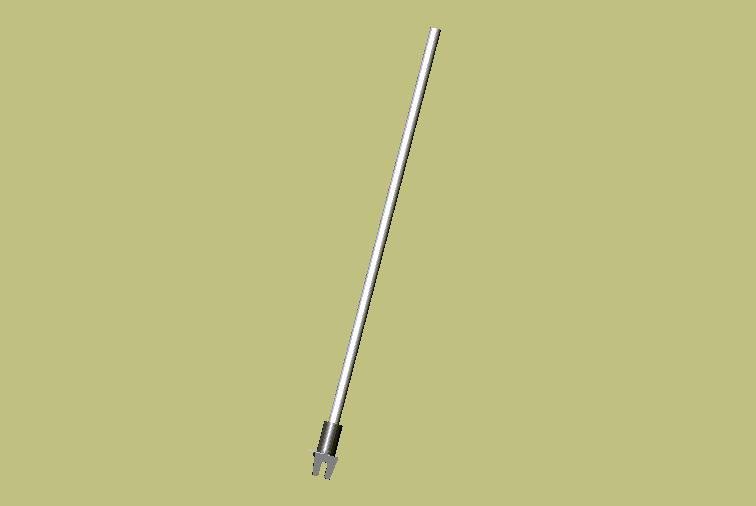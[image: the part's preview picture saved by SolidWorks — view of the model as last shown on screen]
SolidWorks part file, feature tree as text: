
SOLIDWORKS PART (.sldprt)
format: sldprt  version: not decoded by parser v0  size: 140,800 bytes
history: native  units: mm
features: sketch x5, plane x3, extrude x3, cut_extrude x2, material x1, fillet x1 (+8 scaffold rows collapsed)
feature tree (23):
  scaffold x8  (default folders/planes/origin — collapsed)
  material  "Matériau <non spécifié>"
  plane  "Plane1"
  plane  "Plane2"
  plane  "Plane3"
  sketch  "Esquisse1"  dims[D1=7.0mm D2=2.0mm]
  extrude  "Base-Extrusion"  Depth=12mm
  sketch  "Esquisse2"  dims[D1=4.0mm D2=3.0mm]
  extrude  "Boss.-Extru.1"  Depth=150mm
  sketch  "Esquisse3"  dims[D1=4.0mm D2=10.0mm D3=1.5mm D4=1.5mm]
  extrude  "Boss.-Extru.2"  Depth=9mm
  fillet  "Congé1"  Radius=4mm
  sketch  "Esquisse4"  dims[D1=1.0mm]
  cut_extrude  "Enlèv. mat.-Extru.1"  Depth=3mm
  sketch  "Esquisse5"
  cut_extrude  "Enlèv. mat.-Extru.2"  [1 undecoded]
decode coverage: 9 of 11 modeling features carry decoded parameters
note: 1 parameter value undecoded
note: suppression state not decoded; provenance and decode notes live in map.json
